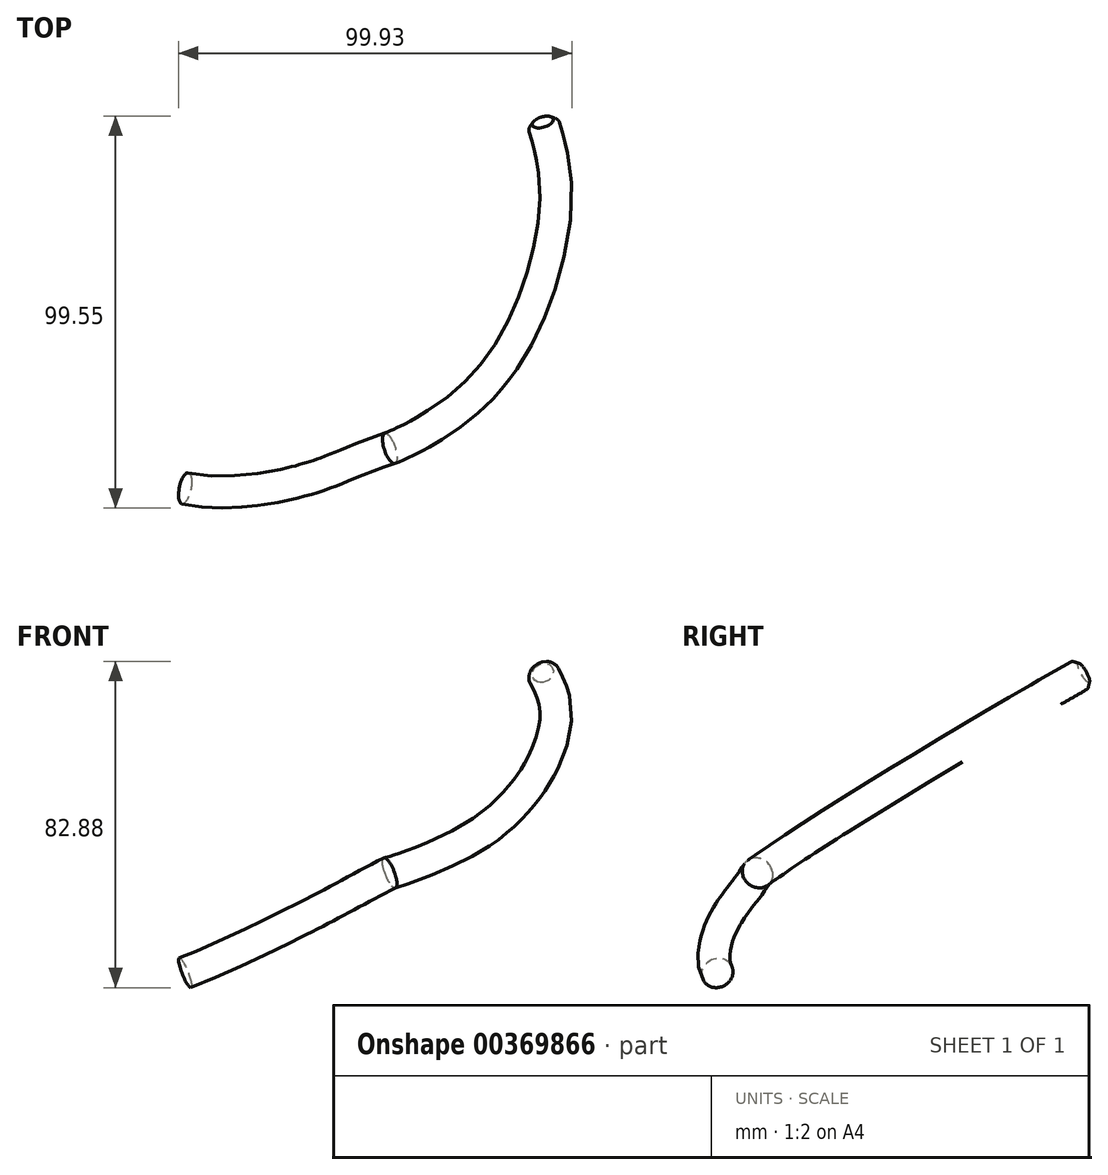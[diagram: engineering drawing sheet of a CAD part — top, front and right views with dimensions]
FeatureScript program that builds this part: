
annotation { "Feature Type Name" : "Feature", "Feature Type Description" : "" }
export const myFeature = defineFeature(function(context is Context, id is Id, definition is map)
    precondition{}
    {
        {
            var Q0;
            Q0=qCreatedBy(makeId("Top.planeOp"),FACE);
            var sketch = newSketch(context, id + "F0", { "sketchPlane" : qUnion([Q0])});
            skPoint(sketch, "E0", {"position": v(-43.63, -40.52) * mm});
            skSolve(sketch);
        }
        {
            var Q0;
            Q0=qCreatedBy(makeId("Top.planeOp"),FACE);
            cPlane(context, id + "F1", {"entities" : qUnion([Q0]), "cplaneType" : CPlaneType.OFFSET, "offset" : 25.4 * mm, "width" : 152.4 * mm, "height" : 152.4 * mm});
        }
        {
            var Q0;
            Q0=qCreatedBy(id+"F1.planeOp",FACE);
            cPlane(context, id + "F2", {"entities" : qUnion([Q0]), "cplaneType" : CPlaneType.OFFSET, "offset" : 25.4 * mm, "width" : 152.4 * mm, "height" : 152.4 * mm});
        }
        {
            var Q0;
            Q0=qCreatedBy(id+"F2.planeOp",FACE);
            cPlane(context, id + "F3", {"entities" : qUnion([Q0]), "cplaneType" : CPlaneType.OFFSET, "offset" : 25.4 * mm, "width" : 152.4 * mm, "height" : 152.4 * mm});
        }
        {
            var Q0;
            Q0=qCreatedBy(id+"F1.planeOp",FACE);
            var sketch = newSketch(context, id + "F4", { "sketchPlane" : qUnion([Q0])});
            skPoint(sketch, "E1", {"position": v(8.35, -30.33) * mm});
            skSolve(sketch);
        }
        {
            var Q0;
            Q0=qCreatedBy(id+"F2.planeOp",FACE);
            var sketch = newSketch(context, id + "F5", { "sketchPlane" : qUnion([Q0])});
            skPoint(sketch, "E2", {"position": v(45.88, 9.36) * mm});
            skSolve(sketch);
        }
        {
            var Q0;
            Q0=qCreatedBy(id+"F3.planeOp",FACE);
            var sketch = newSketch(context, id + "F6", { "sketchPlane" : qUnion([Q0])});
            skPoint(sketch, "E3", {"position": v(47.25, 52.57) * mm});
            skSolve(sketch);
        }
        {
            var Q0;
            Q0=sQuery(id+"F0.wireOp",VERTEX,"E0");
            var Q1;
            Q1=sQuery(id+"F4.wireOp",VERTEX,"E1");
            var Q2;
            Q2=sQuery(id+"F5.wireOp",VERTEX,"E2");
            cPlane(context, id + "F7", {"entities" : qUnion([Q0, Q1, Q2]), "cplaneType" : CPlaneType.THREE_POINT, "offset" : 25.4 * mm, "width" : 152.4 * mm, "height" : 152.4 * mm});
        }
        {
            var Q0;
            Q0=sQuery(id+"F6.wireOp",VERTEX,"E3");
            var Q1;
            Q1=sQuery(id+"F5.wireOp",VERTEX,"E2");
            var Q2;
            Q2=sQuery(id+"F4.wireOp",VERTEX,"E1");
            cPlane(context, id + "F8", {"entities" : qUnion([Q0, Q1, Q2]), "cplaneType" : CPlaneType.THREE_POINT, "offset" : 25.4 * mm, "width" : 152.4 * mm, "height" : 152.4 * mm});
        }
        {
            var Q0;
            Q0=qCreatedBy(id+"F8.planeOp",FACE);
            var sketch = newSketch(context, id + "F9", { "sketchPlane" : qUnion([Q0])});
            skFitSpline(sketch, "E4", {"points": [v(49.11, 83.88) * mm, v(52.22, 56.76) * mm, v(32.86, 4.4) * mm, v(10.17, -13.33) * mm], "startDerivative": vector(25.94, -98.43) * mm, "endDerivative": vector(-19.39, -8.11) * mm});
            skSolve(sketch);
        }
        {
            var Q0;
            Q0=qCreatedBy(id+"F7.planeOp",FACE);
            var sketch = newSketch(context, id + "F10", { "sketchPlane" : qUnion([Q0])});
            skFitSpline(sketch, "E5", {"points": [v(-36.55, 39.58) * mm, v(-1.02, 33.55) * mm, v(20.15, 24.22) * mm], "startDerivative": vector(64.46, 6.97) * mm, "endDerivative": vector(59.5, -23.1) * mm});
            skSolve(sketch);
        }
        {
            var Q0;
            Q0=sQuery(id+"F9.wireOp",EDGE,"E4");
            var Q1;
            Q1=sQuery(id+"F6.wireOp",VERTEX,"E3");
            cPlane(context, id + "F11", {"entities" : qUnion([Q0, Q1]), "cplaneType" : CPlaneType.CURVE_POINT, "offset" : 25.4 * mm, "width" : 152.4 * mm, "height" : 152.4 * mm});
        }
        {
            var Q0;
            Q0=qCreatedBy(id+"F11.planeOp",FACE);
            var sketch = newSketch(context, id + "F12", { "sketchPlane" : qUnion([Q0])});
            skCircle(sketch, "E6", {"center": v(66.9, 40.25) * mm, "radius": 4.04 * mm});
            skSolve(sketch);
        }
        {
            var Q0;
            Q0=makeQuery(id+"F12.imprint","IMPRINT",FACE,{"disambiguationData":[TD([[makeQuery(id+"F12.imprint","IMPRINT",EDGE,{"derivedFrom":sQuery(id+"F12.wireOp",EDGE,"E6")}),1.0]])]});
            var Q1;
            Q1=sQuery(id+"F9.wireOp",EDGE,"E4");
            var Q2;
            Q2=sQuery(id+"F10.wireOp",EDGE,"E5");
            sweep(context, id + "F13", {"profiles" : qUnion([Q0]), "path" : qUnion([Q1, Q2])});
        }
        {
            var Q0;
            Q0=makeQuery(id+"F13.opSweep","CAP_FACE",FACE,{"disambiguationData":[OSD([sQuery(id+"F9.wireOp",VERTEX,"E4.start"),sQuery(id+"F12.wireOp",EDGE,"E6")])],"isStart":true});
            chamfer(context, id + "F14", {"entities" : qUnion([Q0]), "width" : 1.27 * mm, "tangentPropagation" : true});
        }
        {
            var Q0;
            {var subQ0=sQuery(id+"F12.wireOp",EDGE,"E6");Q0=makeQuery(id+"F14.opChamfer","BLEND_EDGE",EDGE,{"blendedFrom":[makeQuery(id+"F13.opSweep","CAP_EDGE",EDGE,{"disambiguationData":[OSD([sQuery(id+"F9.wireOp",VERTEX,"E4.start"),subQ0])],"isStart":true}),makeQuery(id+"F13.opSweep","SWEPT_FACE",FACE,{"disambiguationData":[OSD([sQuery(id+"F9.wireOp",EDGE,"E4"),subQ0])]})],"blendedInto":[makeQuery(id+"F13.opSweep","SWEPT_FACE",FACE,{"disambiguationData":[OSD([sQuery(id+"F9.wireOp",EDGE,"E4"),subQ0])]})]});}
            fillet(context, id + "F15", {"entities" : qUnion([Q0]), "radius" : 0.5 * mm, "tangentPropagation" : true, "allowEdgeOverflow" : false});
        }
    });
